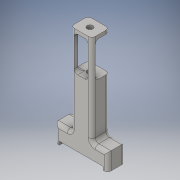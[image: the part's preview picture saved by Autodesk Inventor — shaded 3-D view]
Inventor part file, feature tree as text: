
AUTODESK INVENTOR PART (.ipt)
format: ipt  version: 2016 (Build 200138000, 138)  size: 216,064 bytes
history: native  units: mm
features: sketch x6, extrude x5, projected_geometry x4, fillet x2, hole x1
ambient origin geometry x8: Origin, YZ Plane, XZ Plane, XY Plane, X Axis, Y Axis, Z Axis, Center Point
bodies: Solid1 (feature_tree)
feature tree (18):
  extrude  "Extrusion1"  Depth=30.0mm
  extrude  "Extrusion2"  Depth=12.0mm
  extrude  "Extrusion3"  Depth=8.0mm
  hole  "Hole1"  [1 undecoded]
  extrude  "Extrusion4"  Depth=2.0mm
  extrude  "Extrusion5"  Depth=2.0mm
  fillet  "Fillet1"  Radius=50.0mm
  fillet  "Fillet2"  Radius=2.0mm
  sketch  "Sketch1"  dims[d0=10.0mm d1=30.0mm]
  sketch  "Sketch3"  dims[d2=10.0mm d3=0.0mm d4=12.0mm]
  projected_geometry  "Projected Loop1"
  sketch  "Sketch4"  dims[d5=52.0mm d6=0.0mm d7=8.0mm]
  projected_geometry  "Projected Loop2"
  sketch  "Sketch5"  dims[d8=20.0mm d9=2.0mm]
  sketch  "Sketch6"  dims[d10=50.0mm d11=0.0mm]
  projected_geometry  "Projected Loop3"
  sketch  "Sketch7"  dims[d12=3.3mm d13=6.0mm d14=4.0mm d15=2.0mm d16=90.0deg d17=8.0mm d18=20.594885mm d19=2.0mm d20=2.0mm d21=50.0mm d22=0.0mm d23=2.0mm d24=25.0mm d25=50.0mm d26=0.0mm d27=2.0mm d28=2.0mm]
  projected_geometry  "Projected Loop4"
note: 1 required parameter value undecoded (feature->parameter linkage not recoverable at this tier; creation-order binding heuristic only, values carry confidence <= 0.55)
